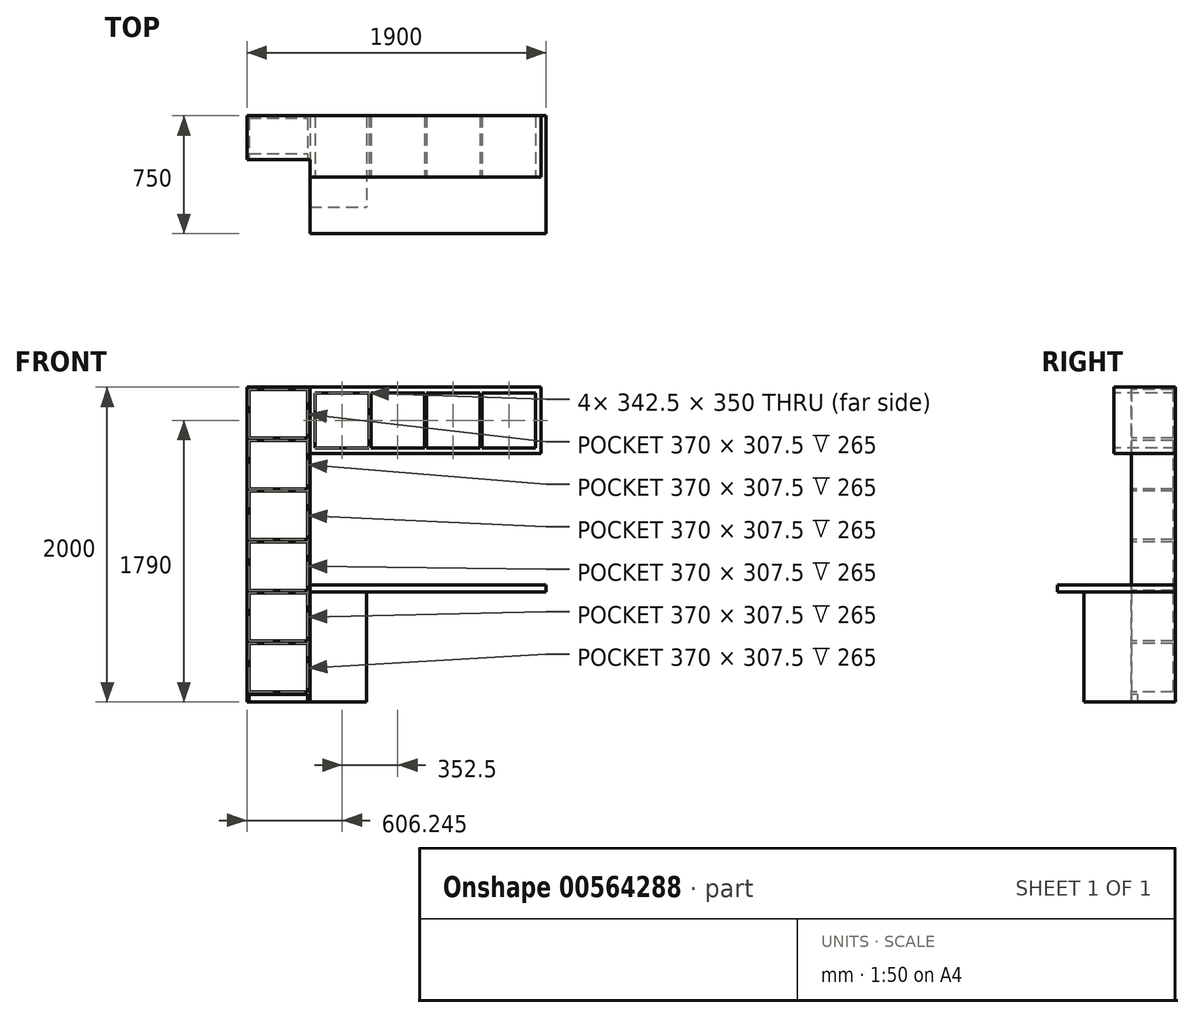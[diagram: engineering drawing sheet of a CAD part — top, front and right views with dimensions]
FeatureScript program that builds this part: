
annotation { "Feature Type Name" : "Feature", "Feature Type Description" : "" }
export const myFeature = defineFeature(function(context is Context, id is Id, definition is map)
    precondition{}
    {
        {
            var Q0;
            Q0=qCreatedBy(makeId("Top.planeOp"),FACE);
            var sketch = newSketch(context, id + "F0", { "sketchPlane" : qUnion([Q0])});
            skLineSegment(sketch, "E0.bottom", {"start": v(-730.93, 374.22) * mm, "end": v(769.07, 374.22) * mm});
            skLineSegment(sketch, "E0.top", {"start": v(-730.93, -375.78) * mm, "end": v(769.07, -375.78) * mm});
            skLineSegment(sketch, "E0.left", {"start": v(-730.93, 374.22) * mm, "end": v(-730.93, -375.78) * mm});
            skLineSegment(sketch, "E0.right", {"start": v(769.07, 374.22) * mm, "end": v(769.07, -375.78) * mm});
            skSolve(sketch);
        }
        {
            var Q0;
            Q0=makeQuery(id+"F0.imprint","IMPRINT",FACE,{"disambiguationData":[TD([[makeQuery(id+"F0.imprint","IMPRINT",EDGE,{"derivedFrom":sQuery(id+"F0.wireOp",EDGE,"E0.bottom")}),-1.0]])]});
            extrude(context, id + "F1", {"entities" : qUnion([Q0]), "depth" : 45 * mm, "offsetDistance" : 25 * mm});
        }
        {
            var Q0;
            Q0=makeQuery(id+"F1.opExtrude","CAP_FACE",FACE,{"disambiguationData":[OSD([sQuery(id+"F0.wireOp",EDGE,"E0.bottom"),sQuery(id+"F0.wireOp",EDGE,"E0.top"),sQuery(id+"F0.wireOp",EDGE,"E0.left"),sQuery(id+"F0.wireOp",EDGE,"E0.right")])],"isStart":true});
            var sketch = newSketch(context, id + "F2", { "sketchPlane" : qUnion([Q0])});
            skLineSegment(sketch, "E1.bottom", {"start": v(-730.93, -374.22) * mm, "end": v(-370.93, -374.22) * mm});
            skLineSegment(sketch, "E1.top", {"start": v(-730.93, 205.78) * mm, "end": v(-370.93, 205.78) * mm});
            skLineSegment(sketch, "E1.left", {"start": v(-730.93, -374.22) * mm, "end": v(-730.93, 205.78) * mm});
            skLineSegment(sketch, "E1.right", {"start": v(-370.93, -374.22) * mm, "end": v(-370.93, 205.78) * mm});
            skSolve(sketch);
        }
        {
            var Q0;
            Q0=makeQuery(id+"F2.imprint","IMPRINT",FACE,{"disambiguationData":[TD([[makeQuery(id+"F2.imprint","IMPRINT",EDGE,{"derivedFrom":sQuery(id+"F2.wireOp",EDGE,"E1.bottom")}),1.0]])]});
            extrude(context, id + "F3", {"entities" : qUnion([Q0]), "depth" : 700 * mm, "offsetDistance" : 25 * mm});
        }
        {
            var Q0;
            Q0=makeQuery(id+"F1.opExtrude","CAP_FACE",FACE,{"disambiguationData":[OSD([sQuery(id+"F0.wireOp",EDGE,"E0.bottom"),sQuery(id+"F0.wireOp",EDGE,"E0.top"),sQuery(id+"F0.wireOp",EDGE,"E0.left"),sQuery(id+"F0.wireOp",EDGE,"E0.right")])],"isStart":true});
            var sketch = newSketch(context, id + "F4", { "sketchPlane" : qUnion([Q0])});
            skSolve(sketch);
        }
        {
            var Q0;
            Q0=makeQuery(id+"F4.imprint","IMPRINT",FACE,{"disambiguationData":[TD([[makeQuery(id+"F4.imprint","IMPRINT",EDGE,{"derivedFrom":makeQuery(id+"F1.opExtrude","CAP_EDGE",EDGE,{"disambiguationData":[OSD([sQuery(id+"F0.wireOp",EDGE,"E0.top")])],"isStart":true})}),-1.0]])]});
            var sketch = newSketch(context, id + "F5", { "sketchPlane" : qUnion([Q0])});
            skCircle(sketch, "E2", {"center": v(719.07, 325.78) * mm, "radius": 20 * mm});
            skCircle(sketch, "E3", {"center": v(719.07, -324.22) * mm, "radius": 20 * mm});
            skSolve(sketch);
        }
        {
            var Q0;
            Q0=sQuery(id+"F5.wireOp",EDGE,"E2");
            extrude(context, id + "F6", {"bodyType" : ToolBodyType.SURFACE, "surfaceEntities" : qUnion([Q0]), "depth" : 700 * mm, "offsetDistance" : 25 * mm});
        }
        {
            var Q0;
            Q0=sQuery(id+"F5.wireOp",EDGE,"E3");
            extrude(context, id + "F7", {"bodyType" : ToolBodyType.SURFACE, "surfaceEntities" : qUnion([Q0]), "depth" : 700 * mm, "offsetDistance" : 25 * mm});
        }
        {
            var Q0;
            Q0=makeQuery(id+"F3.boolean.opBoolean","MERGE",FACE,{"derivedFrom":[makeQuery(id+"F1.opExtrude","SWEPT_FACE",FACE,{"disambiguationData":[OSD([sQuery(id+"F0.wireOp",EDGE,"E0.left")])]}),makeQuery(id+"F3.opExtrude","SWEPT_FACE",FACE,{"disambiguationData":[OSD([sQuery(id+"F2.wireOp",EDGE,"E1.left")])]})]});
            var sketch = newSketch(context, id + "F8", { "sketchPlane" : qUnion([Q0])});
            skLineSegment(sketch, "E4.bottom", {"start": v(-374.22, -700) * mm, "end": v(-94.22, -700) * mm});
            skLineSegment(sketch, "E4.top", {"start": v(-374.22, 1300) * mm, "end": v(-94.22, 1300) * mm});
            skLineSegment(sketch, "E4.left", {"start": v(-374.22, -700) * mm, "end": v(-374.22, 1300) * mm});
            skLineSegment(sketch, "E4.right", {"start": v(-94.22, -700) * mm, "end": v(-94.22, 1300) * mm});
            skSolve(sketch);
        }
        {
            var Q0;
            Q0 = qSketchRegion(id + "F8", true);
            extrude(context, id + "F9", {"entities" : qUnion([Q0]), "depth" : 400 * mm, "offsetDistance" : 25 * mm});
        }
        {
            var Q0;
            Q0=makeQuery(id+"FwZswuIUf6JL1sj_4.boolean.opBoolean","MERGE",FACE,{"derivedFrom":[makeQuery(id+"F9.opExtrude","SWEPT_FACE",FACE,{"disambiguationData":[OSD([sQuery(id+"F8.wireOp",EDGE,"E4.right")])]}),makeQuery(id+"FwZswuIUf6JL1sj_4.opExtrude","SWEPT_FACE",FACE,{"disambiguationData":[OSD([sQuery(id+"FGJRlFmxjeO41BY_4.wireOp",EDGE,"GtMnXYNq-7F83-dHB1-XDAh-mpVRGwtLhi8a.right")])]})]});
            var sketch = newSketch(context, id + "F10", { "sketchPlane" : qUnion([Q0])});
            skLineSegment(sketch, "E5.bottom", {"start": v(-1115.93, 1285) * mm, "end": v(-745.93, 1285) * mm});
            skLineSegment(sketch, "E5.top", {"start": v(-1115.93, 977.5) * mm, "end": v(-745.93, 977.5) * mm});
            skLineSegment(sketch, "E5.left", {"start": v(-1115.93, 1285) * mm, "end": v(-1115.93, 977.5) * mm});
            skLineSegment(sketch, "E5.right", {"start": v(-745.93, 1285) * mm, "end": v(-745.93, 977.5) * mm});
            skLineSegment(sketch, "E6.bottom", {"start": v(-1115.93, 962.5) * mm, "end": v(-745.93, 962.5) * mm});
            skLineSegment(sketch, "E6.top", {"start": v(-1115.93, 655) * mm, "end": v(-745.93, 655) * mm});
            skLineSegment(sketch, "E6.left", {"start": v(-1115.93, 962.5) * mm, "end": v(-1115.93, 655) * mm});
            skLineSegment(sketch, "E6.right", {"start": v(-745.93, 962.5) * mm, "end": v(-745.93, 655) * mm});
            skPoint(sketch, "E7.firstSnap0", {"position": v(-1115.93, 808.75) * mm});
            skLineSegment(sketch, "E7.bottom", {"start": v(-1115.93, 640) * mm, "end": v(-745.93, 640) * mm});
            skLineSegment(sketch, "E7.top", {"start": v(-1115.93, 332.5) * mm, "end": v(-745.93, 332.5) * mm});
            skLineSegment(sketch, "E7.left", {"start": v(-1115.93, 640) * mm, "end": v(-1115.93, 332.5) * mm});
            skLineSegment(sketch, "E7.right", {"start": v(-745.93, 640) * mm, "end": v(-745.93, 332.5) * mm});
            skLineSegment(sketch, "E8.bottom", {"start": v(-1115.93, 317.5) * mm, "end": v(-745.93, 317.5) * mm});
            skLineSegment(sketch, "E8.top", {"start": v(-1115.93, 10) * mm, "end": v(-745.93, 10) * mm});
            skLineSegment(sketch, "E8.left", {"start": v(-1115.93, 317.5) * mm, "end": v(-1115.93, 10) * mm});
            skLineSegment(sketch, "E8.right", {"start": v(-745.93, 317.5) * mm, "end": v(-745.93, 10) * mm});
            skLineSegment(sketch, "E9.bottom", {"start": v(-1115.93, -5) * mm, "end": v(-745.93, -5) * mm});
            skLineSegment(sketch, "E9.top", {"start": v(-1115.93, -312.5) * mm, "end": v(-745.93, -312.5) * mm});
            skLineSegment(sketch, "E9.left", {"start": v(-1115.93, -5) * mm, "end": v(-1115.93, -312.5) * mm});
            skLineSegment(sketch, "E9.right", {"start": v(-745.93, -5) * mm, "end": v(-745.93, -312.5) * mm});
            skLineSegment(sketch, "E10.bottom", {"start": v(-1115.93, -327.5) * mm, "end": v(-745.93, -327.5) * mm});
            skLineSegment(sketch, "E10.top", {"start": v(-1115.93, -635) * mm, "end": v(-745.93, -635) * mm});
            skLineSegment(sketch, "E10.left", {"start": v(-1115.93, -327.5) * mm, "end": v(-1115.93, -635) * mm});
            skLineSegment(sketch, "E10.right", {"start": v(-745.93, -327.5) * mm, "end": v(-745.93, -635) * mm});
            skLineSegment(sketch, "E11.bottom", {"start": v(-1115.93, -650) * mm, "end": v(-745.93, -650) * mm});
            skLineSegment(sketch, "E11.top", {"start": v(-1115.93, -700) * mm, "end": v(-745.93, -700) * mm});
            skLineSegment(sketch, "E11.left", {"start": v(-1115.93, -650) * mm, "end": v(-1115.93, -700) * mm});
            skLineSegment(sketch, "E11.right", {"start": v(-745.93, -650) * mm, "end": v(-745.93, -700) * mm});
            skSolve(sketch);
        }
        {
            var Q0;
            Q0=makeQuery(id+"F10.imprint","IMPRINT",FACE,{"disambiguationData":[TD([[makeQuery(id+"F10.imprint","IMPRINT",EDGE,{"derivedFrom":sQuery(id+"F10.wireOp",EDGE,"E10.bottom")}),-1.0]])]});
            var Q1;
            Q1=makeQuery(id+"F10.imprint","IMPRINT",FACE,{"disambiguationData":[TD([[makeQuery(id+"F10.imprint","IMPRINT",EDGE,{"derivedFrom":sQuery(id+"F10.wireOp",EDGE,"E9.bottom")}),-1.0]])]});
            var Q2;
            Q2=makeQuery(id+"F10.imprint","IMPRINT",FACE,{"disambiguationData":[TD([[makeQuery(id+"F10.imprint","IMPRINT",EDGE,{"derivedFrom":sQuery(id+"F10.wireOp",EDGE,"E8.bottom")}),-1.0]])]});
            var Q3;
            Q3=makeQuery(id+"F10.imprint","IMPRINT",FACE,{"disambiguationData":[TD([[makeQuery(id+"F10.imprint","IMPRINT",EDGE,{"derivedFrom":sQuery(id+"F10.wireOp",EDGE,"E7.bottom")}),-1.0]])]});
            var Q4;
            Q4=makeQuery(id+"F10.imprint","IMPRINT",FACE,{"disambiguationData":[TD([[makeQuery(id+"F10.imprint","IMPRINT",EDGE,{"derivedFrom":sQuery(id+"F10.wireOp",EDGE,"E6.bottom")}),-1.0]])]});
            var Q5;
            Q5=makeQuery(id+"F10.imprint","IMPRINT",FACE,{"disambiguationData":[TD([[makeQuery(id+"F10.imprint","IMPRINT",EDGE,{"derivedFrom":sQuery(id+"F10.wireOp",EDGE,"E5.bottom")}),-1.0]])]});
            extrude(context, id + "F11", {"entities" : qUnion([Q0, Q1, Q2, Q3, Q4, Q5]), "operationType" : NewBodyOperationType.REMOVE, "oppositeDirection" : true, "depth" : 265 * mm, "offsetDistance" : 25 * mm});
        }
        {
            var Q0;
            Q0=makeQuery(id+"F10.imprint","IMPRINT",FACE,{"disambiguationData":[TD([[makeQuery(id+"F10.imprint","IMPRINT",EDGE,{"derivedFrom":sQuery(id+"F10.wireOp",EDGE,"E11.bottom")}),-1.0]])]});
            extrude(context, id + "F12", {"entities" : qUnion([Q0]), "operationType" : NewBodyOperationType.REMOVE, "oppositeDirection" : true, "depth" : 40 * mm, "offsetDistance" : 25 * mm});
        }
        {
            var Q0;
            Q0=makeQuery(id+"F9.opExtrude","CAP_FACE",FACE,{"disambiguationData":[OSD([sQuery(id+"F8.wireOp",EDGE,"E4.bottom"),sQuery(id+"F8.wireOp",EDGE,"E4.top"),sQuery(id+"F8.wireOp",EDGE,"E4.left"),sQuery(id+"F8.wireOp",EDGE,"E4.right")])],"isStart":true});
            var sketch = newSketch(context, id + "F13", { "sketchPlane" : qUnion([Q0])});
            skLineSegment(sketch, "E12.bottom", {"start": v(374.22, 880) * mm, "end": v(-15.78, 880) * mm});
            skLineSegment(sketch, "E12.top", {"start": v(374.22, 1300) * mm, "end": v(-15.78, 1300) * mm});
            skLineSegment(sketch, "E12.left", {"start": v(374.22, 880) * mm, "end": v(374.22, 1300) * mm});
            skLineSegment(sketch, "E12.right", {"start": v(-15.78, 880) * mm, "end": v(-15.78, 1300) * mm});
            skSolve(sketch);
        }
        {
            var Q0;
            {var subQ0=sQuery(id+"F13.wireOp",EDGE,"E12.right");Q0=makeQuery(id+"F13.imprint","IMPRINT",FACE,{"disambiguationData":[TD([[makeQuery(id+"F13.imprint","IMPRINT",EDGE,{"derivedFrom":subQ0}),-1.0]])]});}
            var Q1;
            {var subQ0=sQuery(id+"F13.wireOp",EDGE,"E12.left");Q1=makeQuery(id+"F13.imprint","IMPRINT",FACE,{"disambiguationData":[TD([[makeQuery(id+"F13.imprint","IMPRINT",EDGE,{"derivedFrom":subQ0}),1.0]])]});}
            extrude(context, id + "F14", {"entities" : qUnion([Q0, Q1]), "operationType" : NewBodyOperationType.ADD, "depth" : 1470 * mm, "offsetDistance" : 25 * mm});
        }
        {
            var Q0;
            Q0=makeQuery(id+"F14.opExtrude","SWEPT_FACE",FACE,{"disambiguationData":[OSD([sQuery(id+"F13.wireOp",EDGE,"E12.right")])]});
            var sketch = newSketch(context, id + "F15", { "sketchPlane" : qUnion([Q0])});
            skLineSegment(sketch, "E13.bottom", {"start": v(-695.93, 1265) * mm, "end": v(-353.43, 1265) * mm});
            skLineSegment(sketch, "E13.top", {"start": v(-695.93, 915) * mm, "end": v(-353.43, 915) * mm});
            skLineSegment(sketch, "E13.left", {"start": v(-695.93, 1265) * mm, "end": v(-695.93, 915) * mm});
            skLineSegment(sketch, "E13.right", {"start": v(-353.43, 1265) * mm, "end": v(-353.43, 915) * mm});
            skLineSegment(sketch, "E14.bottom", {"start": v(-343.43, 1265) * mm, "end": v(-0.93, 1265) * mm});
            skLineSegment(sketch, "E14.top", {"start": v(-343.43, 915) * mm, "end": v(-0.93, 915) * mm});
            skLineSegment(sketch, "E14.left", {"start": v(-343.43, 1265) * mm, "end": v(-343.43, 915) * mm});
            skLineSegment(sketch, "E14.right", {"start": v(-0.93, 1265) * mm, "end": v(-0.93, 915) * mm});
            skLineSegment(sketch, "E15.bottom", {"start": v(9.07, 1265) * mm, "end": v(351.57, 1265) * mm});
            skLineSegment(sketch, "E15.top", {"start": v(9.07, 915) * mm, "end": v(351.57, 915) * mm});
            skLineSegment(sketch, "E15.left", {"start": v(9.07, 1265) * mm, "end": v(9.07, 915) * mm});
            skLineSegment(sketch, "E15.right", {"start": v(351.57, 1265) * mm, "end": v(351.57, 915) * mm});
            skLineSegment(sketch, "E16.bottom", {"start": v(361.57, 1265) * mm, "end": v(704.07, 1265) * mm});
            skLineSegment(sketch, "E16.top", {"start": v(361.57, 915) * mm, "end": v(704.07, 915) * mm});
            skLineSegment(sketch, "E16.left", {"start": v(361.57, 1265) * mm, "end": v(361.57, 915) * mm});
            skLineSegment(sketch, "E16.right", {"start": v(704.07, 1265) * mm, "end": v(704.07, 915) * mm});
            skSolve(sketch);
        }
        {
            var Q0;
            Q0=makeQuery(id+"F15.imprint","IMPRINT",FACE,{"disambiguationData":[TD([[makeQuery(id+"F15.imprint","IMPRINT",EDGE,{"derivedFrom":sQuery(id+"F15.wireOp",EDGE,"E13.bottom")}),-1.0]])]});
            var Q1;
            Q1=makeQuery(id+"F15.imprint","IMPRINT",FACE,{"disambiguationData":[TD([[makeQuery(id+"F15.imprint","IMPRINT",EDGE,{"derivedFrom":sQuery(id+"F15.wireOp",EDGE,"E14.bottom")}),-1.0]])]});
            var Q2;
            Q2=makeQuery(id+"F15.imprint","IMPRINT",FACE,{"disambiguationData":[TD([[makeQuery(id+"F15.imprint","IMPRINT",EDGE,{"derivedFrom":sQuery(id+"F15.wireOp",EDGE,"E15.bottom")}),-1.0]])]});
            var Q3;
            Q3=makeQuery(id+"F15.imprint","IMPRINT",FACE,{"disambiguationData":[TD([[makeQuery(id+"F15.imprint","IMPRINT",EDGE,{"derivedFrom":sQuery(id+"F15.wireOp",EDGE,"E16.bottom")}),-1.0]])]});
            extrude(context, id + "F16", {"entities" : qUnion([Q0, Q1, Q2, Q3]), "operationType" : NewBodyOperationType.REMOVE, "oppositeDirection" : true, "depth" : 390 * mm, "offsetDistance" : 25 * mm});
        }
    });
